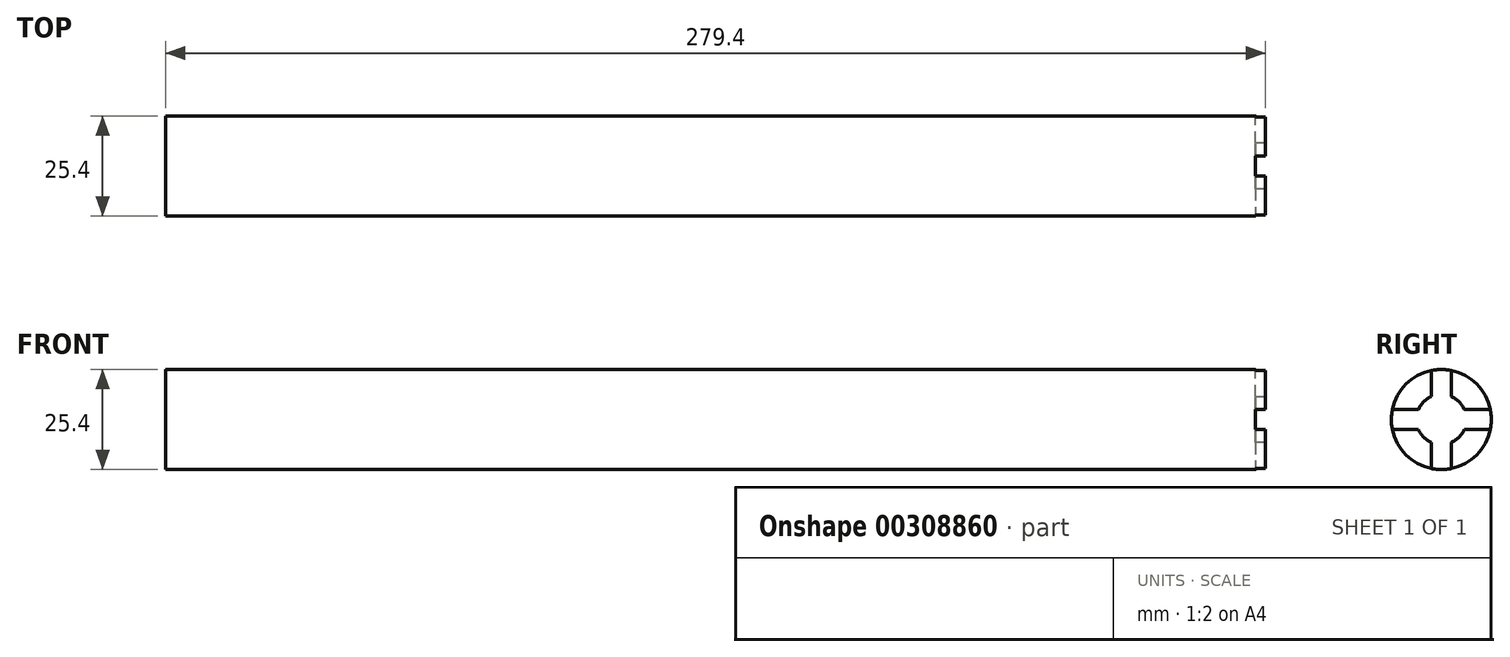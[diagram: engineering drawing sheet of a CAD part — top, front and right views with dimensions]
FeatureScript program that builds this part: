
annotation { "Feature Type Name" : "Feature", "Feature Type Description" : "" }
export const myFeature = defineFeature(function(context is Context, id is Id, definition is map)
    precondition{}
    {
        {
            var Q0;
            Q0=qCreatedBy(makeId("Right.planeOp"),FACE);
            var sketch = newSketch(context, id + "F0", { "sketchPlane" : qUnion([Q0])});
            skCircle(sketch, "E0", {"center": v(0, 0) * mm, "radius": 12.7 * mm});
            skSolve(sketch);
        }
        {
            var Q0;
            Q0 = qSketchRegion(id + "F0", true);
            extrude(context, id + "F1", {"entities" : qUnion([Q0]), "depth" : 279.4 * mm});
        }
        {
            var Q0;
            Q0=makeQuery(id+"F1.opExtrude","CAP_FACE",FACE,{"disambiguationData":[OSD([sQuery(id+"F0.wireOp",EDGE,"E0")])],"isStart":false});
            var sketch = newSketch(context, id + "F2", { "sketchPlane" : qUnion([Q0])});
            skCircle(sketch, "E1", {"center": v(0, 0) * mm, "radius": 6.35 * mm});
            skSolve(sketch);
        }
        {
            var Q0;
            Q0 = qSketchRegion(id + "F2", true);
            extrude(context, id + "F3", {"entities" : qUnion([Q0]), "operationType" : NewBodyOperationType.REMOVE, "oppositeDirection" : true, "depth" : 2.54 * mm});
        }
        {
            var Q0;
            Q0=makeQuery(id+"F1.opExtrude","CAP_FACE",FACE,{"disambiguationData":[OSD([sQuery(id+"F0.wireOp",EDGE,"E0")])],"isStart":false});
            var sketch = newSketch(context, id + "F4", { "sketchPlane" : qUnion([Q0])});
            skLineSegment(sketch, "E2", {"start": v(2.54, 5.82) * mm, "end": v(2.54, 22.74) * mm});
            skLineSegment(sketch, "E3", {"start": v(2.54, 22.74) * mm, "end": v(0, 22.74) * mm});
            skLineSegment(sketch, "E4", {"start": v(2.54, -5.82) * mm, "end": v(2.54, -26.6) * mm});
            skLineSegment(sketch, "E5", {"start": v(2.54, -26.6) * mm, "end": v(0, -26.6) * mm});
            skLineSegment(sketch, "E6", {"start": v(5.82, 2.54) * mm, "end": v(28.84, 2.54) * mm});
            skLineSegment(sketch, "E7", {"start": v(28.84, 2.54) * mm, "end": v(28.84, 0) * mm});
            skLineSegment(sketch, "E8", {"start": v(-5.82, 2.54) * mm, "end": v(-28.23, 2.54) * mm});
            skLineSegment(sketch, "E9", {"start": v(-28.23, 2.54) * mm, "end": v(-28.23, 0) * mm});
            skLineSegment(sketch, "E10.MirrorCS", {"start": v(-2.54, 5.82) * mm, "end": v(-2.54, 22.74) * mm});
            skLineSegment(sketch, "E11.MirrorCS", {"start": v(-2.54, 22.74) * mm, "end": v(0, 22.74) * mm});
            skLineSegment(sketch, "E12.MirrorCS", {"start": v(-2.54, -5.82) * mm, "end": v(-2.54, -26.6) * mm});
            skLineSegment(sketch, "E13.MirrorCS", {"start": v(-2.54, -26.6) * mm, "end": v(0, -26.6) * mm});
            skLineSegment(sketch, "E14.MirrorCS", {"start": v(-5.82, -2.54) * mm, "end": v(-28.23, -2.54) * mm});
            skLineSegment(sketch, "E15.MirrorCS", {"start": v(-28.23, -2.54) * mm, "end": v(-28.23, 0) * mm});
            skLineSegment(sketch, "E16.MirrorCS", {"start": v(5.82, -2.54) * mm, "end": v(28.84, -2.54) * mm});
            skLineSegment(sketch, "E17.MirrorCS", {"start": v(28.84, -2.54) * mm, "end": v(28.84, 0) * mm});
            skCircle(sketch, "E18", {"center": v(0, 0) * mm, "radius": 6.35 * mm});
            skSolve(sketch);
        }
        {
            var Q0;
            Q0 = qSketchRegion(id + "F4", true);
            extrude(context, id + "F5", {"entities" : qUnion([Q0]), "operationType" : NewBodyOperationType.REMOVE, "oppositeDirection" : true, "depth" : 2.54 * mm});
        }
    });
